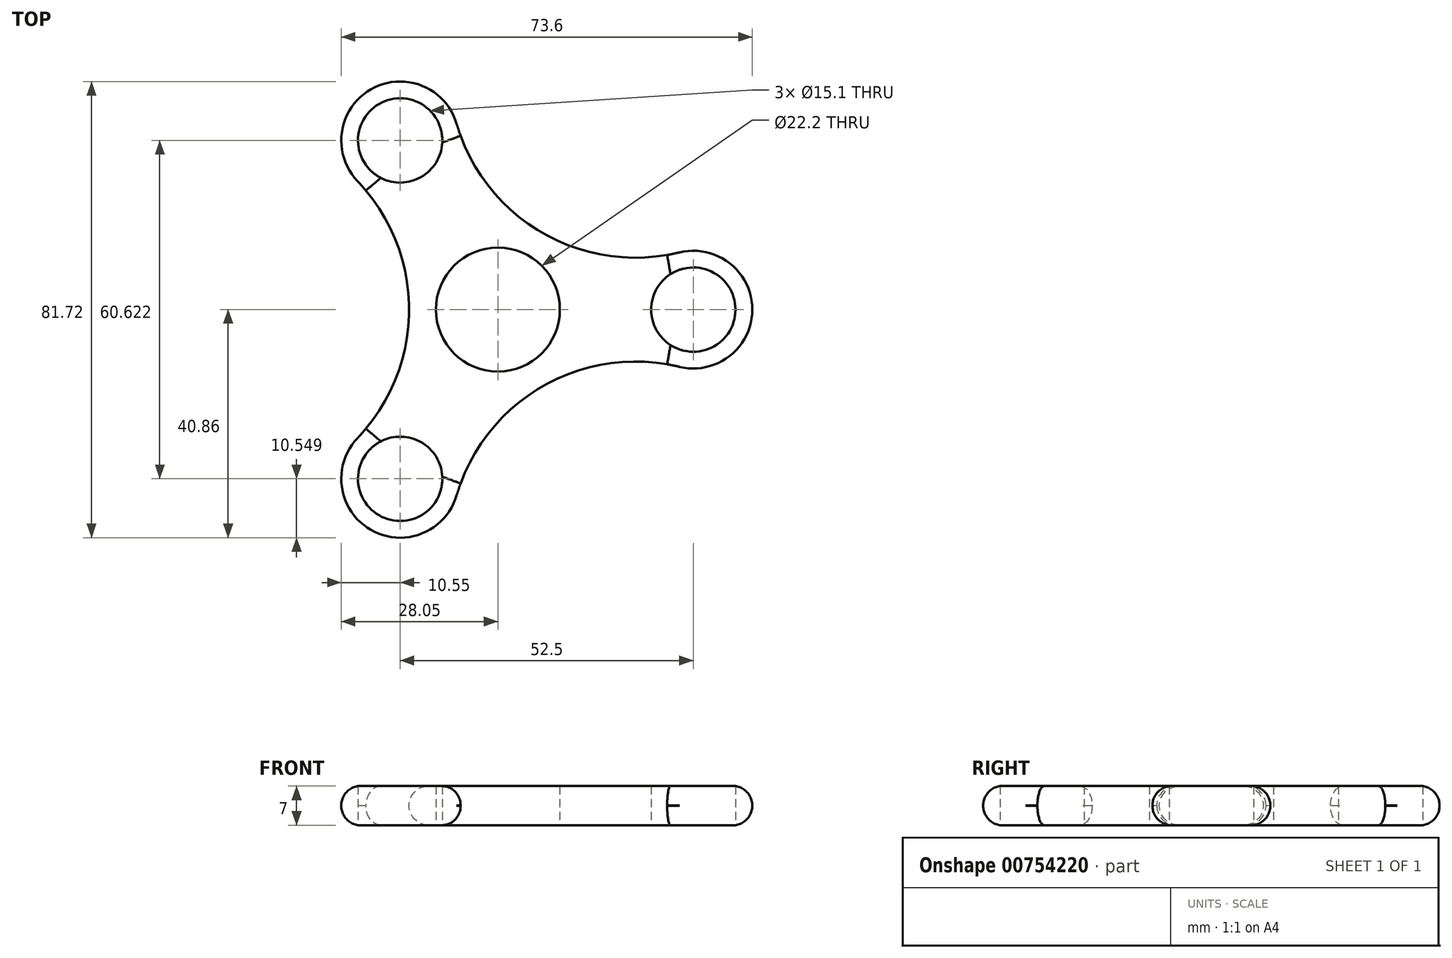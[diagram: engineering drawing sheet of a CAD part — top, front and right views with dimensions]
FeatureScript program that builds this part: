
annotation { "Feature Type Name" : "Feature", "Feature Type Description" : "" }
export const myFeature = defineFeature(function(context is Context, id is Id, definition is map)
    precondition{}
    {
        {
            var Q0;
            Q0=qCreatedBy(makeId("Top.planeOp"),FACE);
            var sketch = newSketch(context, id + "F0", { "sketchPlane" : qUnion([Q0])});
            skCircle(sketch, "E0", {"center": v(0, 0) * mm, "radius": 11.1 * mm});
            skCircle(sketch, "E1", {"center": v(35, 0) * mm, "radius": 7.55 * mm});
            skCircle(sketch, "E2.0", {"center": v(35, 0) * mm, "radius": 10.55 * mm});
            skCircle(sketch, "E3.1.0", {"center": v(-17.5, 30.31) * mm, "radius": 10.55 * mm});
            skCircle(sketch, "E3.1.1", {"center": v(-17.5, 30.31) * mm, "radius": 7.55 * mm});
            skCircle(sketch, "E3.2.0", {"center": v(-17.5, -30.31) * mm, "radius": 10.55 * mm});
            skCircle(sketch, "E3.2.1", {"center": v(-17.5, -30.31) * mm, "radius": 7.55 * mm});
            skArc(sketch, "E4", {"start": v(-7.37, 33.27) * mm, "mid": v(7.95, 13.77) * mm, "end": v(32.5, 10.25) * mm});
            skArc(sketch, "E5.1.0", {"start": v(-25.13, -23.02) * mm, "mid": v(-15.9, 0) * mm, "end": v(-25.13, 23.02) * mm});
            skArc(sketch, "E5.2.0", {"start": v(32.5, -10.25) * mm, "mid": v(7.95, -13.77) * mm, "end": v(-7.37, -33.27) * mm});
            skSolve(sketch);
        }
        {
            var Q0;
            Q0=makeQuery(id+"F0.imprint","IMPRINT",FACE,{"disambiguationData":[TD([[makeQuery(id+"F0.imprint","IMPRINT",EDGE,{"derivedFrom":sQuery(id+"F0.wireOp",EDGE,"E0")}),-1.0]])]});
            var Q1;
            Q1=makeQuery(id+"F0.imprint","IMPRINT",FACE,{"disambiguationData":[TD([[makeQuery(id+"F0.imprint","IMPRINT",EDGE,{"derivedFrom":sQuery(id+"F0.wireOp",EDGE,"E3.1.1")}),-1.0]])]});
            var Q2;
            Q2=makeQuery(id+"F0.imprint","IMPRINT",FACE,{"disambiguationData":[TD([[makeQuery(id+"F0.imprint","IMPRINT",EDGE,{"derivedFrom":sQuery(id+"F0.wireOp",EDGE,"E1")}),-1.0]])]});
            var Q3;
            Q3=makeQuery(id+"F0.imprint","IMPRINT",FACE,{"disambiguationData":[TD([[makeQuery(id+"F0.imprint","IMPRINT",EDGE,{"derivedFrom":sQuery(id+"F0.wireOp",EDGE,"E3.2.1")}),-1.0]])]});
            extrude(context, id + "F1", {"entities" : qUnion([Q0, Q1, Q2, Q3]), "depth" : 7 * mm, "offsetDistance" : 25 * mm});
        }
        {
            var Q0;
            Q0=makeQuery(id+"F1.opExtrude","CAP_EDGE",EDGE,{"disambiguationData":[OSD([sQuery(id+"F0.wireOp",EDGE,"E5.1.0")])],"isStart":false});
            var Q1;
            Q1=makeQuery(id+"F1.opExtrude","CAP_EDGE",EDGE,{"disambiguationData":[OSD([sQuery(id+"F0.wireOp",EDGE,"E5.1.0")])],"isStart":true});
            fillet(context, id + "F2", {"entities" : qUnion([Q0, Q1]), "radius" : 3.5 * mm, "tangentPropagation" : true, "allowEdgeOverflow" : false});
        }
    });
